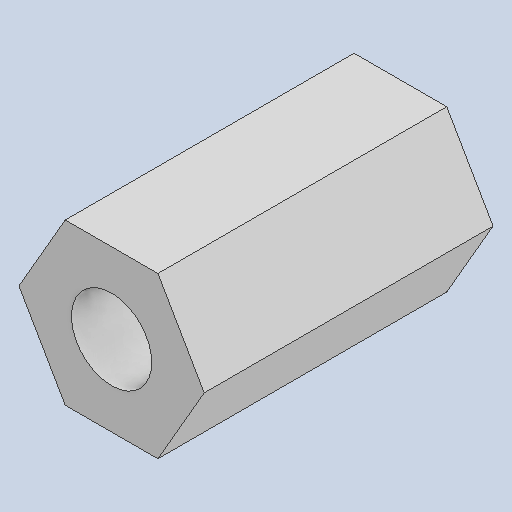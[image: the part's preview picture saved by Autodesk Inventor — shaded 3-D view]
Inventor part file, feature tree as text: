
AUTODESK INVENTOR PART (.ipt)
format: ipt  version: 2024.2 (Build 282272000, 272)  size: 102,400 bytes
history: native  units: mm
features: extrude x2, sketch x1
ambient origin geometry x8: Origin, YZ Plane, XZ Plane, XY Plane, X Axis, Y Axis, Z Axis, Center Point
bodies: Solid1 (feature_tree)
feature tree (3):
  extrude  "Extrusion1"  Depth=9.0mm TaperAngle=0.0deg
  extrude  "Extrusion3"  Depth=9.0mm
  sketch  "Sketch1"  dims[d0=5.0mm d1=9.0mm d2=0.0mm d6=2.5mm d7=7.0mm d8=0.0mm]
